# Revit family: 1BasicPlus2_RFA
name_source: partatom
category: Data Devices
units: mm (PartAtom-declared; Revit-internal decimal feet)

## family parameters
Cut with Voids When Loaded = No
Host = Face
Maintain Annotation Orientation = Yes
Part Type = Normal
Room Calculation Point = No
Round Connector Dimension = Use Diameter
Shared = No

## types (6) — shared parameters
Body Material = Danfoss Plastic White
Description = Main Controller and Room Thermostat
H1 = 43 mm  [stored 0.141076 ft]
IP Rating = IP30
IfcExportAs = IfcElectricApplianceType
IfcExportType = BasicPlus2
In wall Bottom(200) = No
L1 = 43 mm  [stored 0.141076 ft]
L2_In wall bottom = 25 mm  [stored 0.082021 ft]
L3 = 83.8 mm
L4 = 86 mm  [stored 0.282152 ft]
LOD 200 = No
LOD 350 = Yes
L_blend base = 86 mm  [stored 0.282152 ft]
L_blend top = 72 mm  [stored 0.23622 ft]
L_bottom plate = 72 mm  [stored 0.23622 ft]
Manufacturer = Danfoss
Max Ambient Temperature = 60 °C
Min Temperature Setting = 5 °C
Operating Frequency = 50/60 Hz
R1 = 2 mm  [stored 0.00656168 ft]
R2 = 4 mm  [stored 0.0131234 ft]
RN = 2 mm  [stored 0.00656168 ft]
URL = https://store.danfoss.com
Voltage = 230 V
W2 = 24.5 mm
W3 = 6 mm  [stored 0.019685 ft]
W4 = 6 mm  [stored 0.019685 ft]
W_extrusion = 3 mm  [stored 0.00984252 ft]
zero-valued in all types: Default Elevation

## per-type parameters (varying)
| type | Bottom 50x50 | Bottom_DR_PR(350) | Bottom_D_P(350) | Communication Interface | Communication Protocol | Fault Indication | H1_In wall Bottom | In wall | L1_In wall bottom | LCD backlight | Max Temperature Setting | Model | Model Type | Operating Floor Temperature Range | Operating Temperature Range | Power | Power Consumption | Power Supply RT | W1 | W_blend | Weight |
| BasicPlus2_In-wall_WT-D_Display_088U0622 | 1 mm  [stored 0.00328084 ft] | No | Yes | - | - | Yes | 50 mm  [stored 0.164042 ft] | 1 mm  [stored 0.00328084 ft] | 50 mm  [stored 0.164042 ft] | Yes, white | 35 °C | 088U0622,088U0623 | BasicPlus2_In-wall_WT-D_Display | Off, 20 °C to 45 °C | Off, 5 °C to 35 °C | 2 VA | 2 W | 85-250 VAC | 16 mm | 4 mm  [stored 0.0131234 ft] | 0.13 kg |
| BasicPlus2_In-wall_WT-DM_Display and RS485_088U0627 | 0 mm  [stored 0 ft] | Yes | No | RS485 | Modbus RTU | Yes | 50 mm  [stored 0.164042 ft] | 1 mm  [stored 0.00328084 ft] | 50 mm  [stored 0.164042 ft] | Yes, white | 35 °C | 088U0627 | BasicPlus2_In-wall_WT-DM_Display and RS485 | Off, 20 °C to 45 °C | Off, 5 °C to 35 °C | 2 VA | 2 W | 85-250 VAC | 16 mm | 4 mm  [stored 0.0131234 ft] | 0.19 kg |
| BasicPlus2_In-wall_WT-DR_Display and Relay_088U0624 | 0 mm  [stored 0 ft] | Yes | No | - | - | Yes | 62.3 mm  [stored 0.204396 ft] | 1 mm  [stored 0.00328084 ft] | 46.2 mm  [stored 0.151575 ft] | Yes, white | 35 °C | 088U0624 | BasicPlus2_In-wall_WT-DR_Display and Relay | Off, 20 °C to 45 °C | Off, 5 °C to 35 °C | 2 VA | 2 W | 85-250 VAC | 16 mm | 4 mm  [stored 0.0131234 ft] | 0.21 kg |
| BasicPlus2_In-wall_WT-P_Programmable_088U0625 | 1 mm  [stored 0.00328084 ft] | No | Yes | - | - | Yes | 50 mm  [stored 0.164042 ft] | 1 mm  [stored 0.00328084 ft] | 50 mm  [stored 0.164042 ft] | Yes, white | 35 °C | 088U0625 | BasicPlus2_In-wall_WT-P_Programmable | Off, 20 °C to 45 °C | Off, 5 °C to 35 °C | 2 VA | 2 W | 85-250 VAC | 16 mm | 4 mm  [stored 0.0131234 ft] | 0.13 kg |
| BasicPlus2_In-wall_WT-PR_Programmable and Relay_088U0626 | 0 mm  [stored 0 ft] | Yes | No | - | - | Yes | 62.3 mm  [stored 0.204396 ft] | 1 mm  [stored 0.00328084 ft] | 46.2 mm  [stored 0.151575 ft] | Yes, white | 35 °C | 088U0626 | BasicPlus2_In-wall_WT-PR_Programmable and Relay | Off, 20 °C to 45 °C | Off, 5 °C to 35 °C | 2 VA | 2 W | 85-250 VAC | 16 mm | 4 mm  [stored 0.0131234 ft] | 0.21 kg |
| BasicPlus2_On-wall_WT-T_Toggle_088U0620 | 0 mm  [stored 0 ft] | No | No | - | - | - | 62.3 mm  [stored 0.204396 ft] | 0 mm  [stored 0 ft] | 46.2 mm  [stored 0.151575 ft] | - | 30 °C | 088U0620,088U0621 | BasicPlus2_On-wall_WT-T_Toggle | - | Off, 5 °C to 30 °C | 7 VA | 7 W | 230 VAC | 30 mm  [stored 0.0984252 ft] | 18 mm  [stored 0.0590551 ft] | 0.10 kg |

note: [stored X ft] marks values corroborated as IEEE doubles in the binary element streams (Revit-internal decimal feet)

## geometry (parser evidence)
native form markers: Sweep x3
no freeform markers — native parametric forms only
